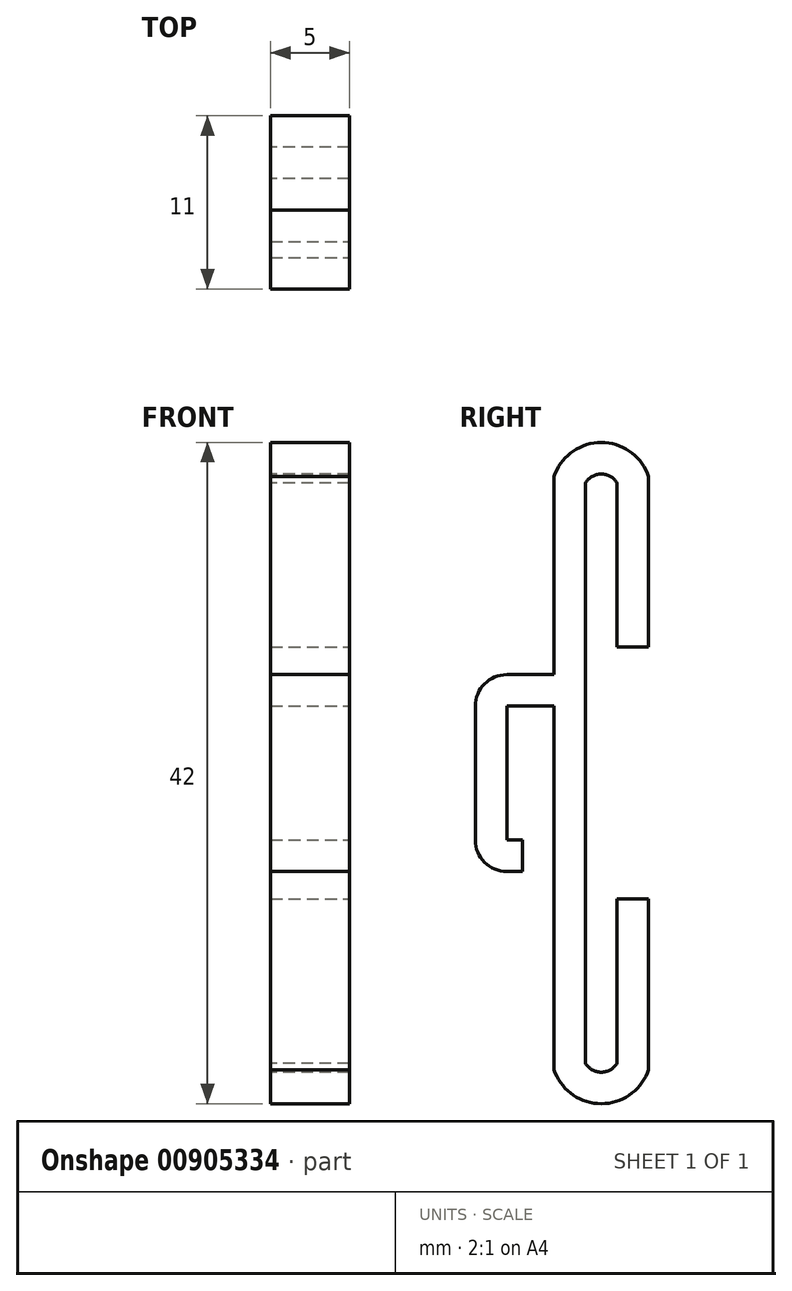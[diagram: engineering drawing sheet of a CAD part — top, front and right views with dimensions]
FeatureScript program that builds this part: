
annotation { "Feature Type Name" : "Feature", "Feature Type Description" : "" }
export const myFeature = defineFeature(function(context is Context, id is Id, definition is map)
    precondition{}
    {
        {
            assignVariable(context, id + "F0", {"name" : "thickness", "anyValue" : 2 * mm});
        }
        {
            var Q0;
            Q0=qCreatedBy(makeId("Right.planeOp"),FACE);
            var sketch = newSketch(context, id + "F1", { "sketchPlane" : qUnion([Q0])});
            skArc(sketch, "E0", {"start": v(4, 18.65) * mm, "mid": v(2, 20) * mm, "end": v(0, 18.65) * mm});
            skLineSegment(sketch, "E1", {"start": v(0, 18.65) * mm, "end": v(0, 0) * mm});
            skLineSegment(sketch, "E2", {"start": v(4, 18.65) * mm, "end": v(4, 8) * mm});
            skLineSegment(sketch, "E3", {"start": v(2, 20) * mm, "end": v(-23.66, 20) * mm, "construction": true});
            skLineSegment(sketch, "E4", {"start": v(2, 20) * mm, "end": v(20.62, 20) * mm, "construction": true});
            skLineSegment(sketch, "E5.MirrorCS", {"start": v(0, -18.65) * mm, "end": v(0, 0) * mm});
            skArc(sketch, "E6.MirrorCS", {"start": v(4, -18.65) * mm, "mid": v(2, -20) * mm, "end": v(0, -18.65) * mm});
            skLineSegment(sketch, "E7.MirrorCS", {"start": v(4, -18.65) * mm, "end": v(4, -8) * mm});
            skLineSegment(sketch, "E8", {"start": v(2, 20) * mm, "end": v(2, 17.84) * mm, "construction": true});
            skLineSegment(sketch, "E9", {"start": v(0, 18.65) * mm, "end": v(4, 18.65) * mm, "construction": true});
            skSolve(sketch);
        }
        {
            var Q0;
            Q0=qCreatedBy(makeId("Top.planeOp"),FACE);
            var sketch = newSketch(context, id + "F2", { "sketchPlane" : qUnion([Q0])});
            skLineSegment(sketch, "E10.bottom", {"start": v(-2.5, 1) * mm, "end": v(2.5, 1) * mm});
            skLineSegment(sketch, "E10.top", {"start": v(-2.5, -1) * mm, "end": v(2.5, -1) * mm});
            skLineSegment(sketch, "E10.left", {"start": v(-2.5, 1) * mm, "end": v(-2.5, -1) * mm});
            skLineSegment(sketch, "E10.right", {"start": v(2.5, 1) * mm, "end": v(2.5, -1) * mm});
            skLineSegment(sketch, "E11", {"start": v(2.5, 1) * mm, "end": v(-2.5, -1) * mm, "construction": true});
            skPoint(sketch, "E12", {"position": v(0, 0) * mm});
            skSolve(sketch);
        }
        {
            var Q0;
            Q0=makeQuery(id+"F2.imprint","IMPRINT",FACE,{"disambiguationData":[TD([[makeQuery(id+"F2.imprint","IMPRINT",EDGE,{"derivedFrom":sQuery(id+"F2.wireOp",EDGE,"E10.bottom")}),-1.0]])]});
            var Q1;
            Q1=sQuery(id+"F1.wireOp",EDGE,"E1");
            var Q2;
            Q2=sQuery(id+"F1.wireOp",EDGE,"E0");
            var Q3;
            Q3=sQuery(id+"F1.wireOp",EDGE,"E2");
            var Q4;
            Q4=sQuery(id+"F1.wireOp",EDGE,"E7.MirrorCS");
            var Q5;
            Q5=sQuery(id+"F1.wireOp",EDGE,"E6.MirrorCS");
            var Q6;
            Q6=sQuery(id+"F1.wireOp",EDGE,"E5.MirrorCS");
            sweep(context, id + "F3", {"profiles" : qUnion([Q0]), "path" : qUnion([Q1, Q2, Q3, Q4, Q5, Q6])});
        }
        {
            assignVariable(context, id + "F4", {"name" : "led_height", "anyValue" : 3 * mm});
        }
        {
            var Q0;
            Q0=makeQuery(id+"F3.opSweep","SWEPT_FACE",FACE,{"disambiguationData":[OSD([sQuery(id+"F1.wireOp",EDGE,"E1"),sQuery(id+"F2.wireOp",EDGE,"E10.top")])]});
            var sketch = newSketch(context, id + "F5", { "sketchPlane" : qUnion([Q0])});
            skLineSegment(sketch, "E13.bottom", {"start": v(-2.5, -6.25) * mm, "end": v(2.5, -6.25) * mm});
            skLineSegment(sketch, "E13.top", {"start": v(-2.5, 6.25) * mm, "end": v(2.5, 6.25) * mm});
            skLineSegment(sketch, "E13.left", {"start": v(-2.5, -6.25) * mm, "end": v(-2.5, 6.25) * mm});
            skLineSegment(sketch, "E13.right", {"start": v(2.5, -6.25) * mm, "end": v(2.5, 6.25) * mm});
            skLineSegment(sketch, "E14", {"start": v(-2.5, -6.25) * mm, "end": v(2.5, 6.25) * mm, "construction": true});
            skPoint(sketch, "E15", {"position": v(0, 0) * mm});
            skSolve(sketch);
        }
        {
            var Q0;
            Q0=makeQuery(id+"F5.imprint","IMPRINT",FACE,{"disambiguationData":[TD([[makeQuery(id+"F5.imprint","IMPRINT",EDGE,{"derivedFrom":sQuery(id+"F5.wireOp",EDGE,"E13.bottom")}),1.0]])]});
            extrude(context, id + "F6", {"entities" : qUnion([Q0]), "operationType" : NewBodyOperationType.ADD, "depth" : getVariable(context, 'led_height') + getVariable(context, 'thickness'), "offsetDistance" : 25 * mm});
        }
        {
            var Q0;
            Q0=makeQuery(id+"F6.boolean.opBoolean","MERGE",FACE,{"derivedFrom":[makeQuery(id+"F3.opSweep","SWEPT_FACE",FACE,{"disambiguationData":[OSD([sQuery(id+"F1.wireOp",EDGE,"E7.MirrorCS"),sQuery(id+"F2.wireOp",EDGE,"E10.right")])]}),makeQuery(id+"F6.opExtrude","SWEPT_FACE",FACE,{"disambiguationData":[OSD([sQuery(id+"F5.wireOp",EDGE,"E13.right")])]})]});
            var sketch = newSketch(context, id + "F7", { "sketchPlane" : qUnion([Q0])});
            skLineSegment(sketch, "E16.bottom", {"start": v(-4, -4.25) * mm, "end": v(-1, -4.25) * mm});
            skLineSegment(sketch, "E16.top", {"start": v(-4, 4.25) * mm, "end": v(-1, 4.25) * mm});
            skLineSegment(sketch, "E16.left", {"start": v(-4, -4.25) * mm, "end": v(-4, 4.25) * mm});
            skLineSegment(sketch, "E16.right", {"start": v(-1, -4.25) * mm, "end": v(-1, 4.25) * mm});
            skLineSegment(sketch, "E17", {"start": v(-4, -4.25) * mm, "end": v(-1, 4.25) * mm, "construction": true});
            skPoint(sketch, "E18", {"position": v(-2.5, 0) * mm});
            skSolve(sketch);
        }
        {
            var Q0;
            Q0=makeQuery(id+"F7.imprint","IMPRINT",FACE,{"disambiguationData":[TD([[makeQuery(id+"F7.imprint","IMPRINT",EDGE,{"derivedFrom":sQuery(id+"F7.wireOp",EDGE,"E16.bottom")}),1.0]])]});
            extrude(context, id + "F8", {"entities" : qUnion([Q0]), "operationType" : NewBodyOperationType.REMOVE, "endBound" : BoundingType.THROUGH_ALL, "oppositeDirection" : true, "depth" : 25 * mm, "offsetDistance" : 25 * mm});
        }
        {
            var Q0;
            Q0=makeQuery(id+"F6.opExtrude","SWEPT_FACE",FACE,{"disambiguationData":[OSD([sQuery(id+"F5.wireOp",EDGE,"E13.bottom")])]});
            var sketch = newSketch(context, id + "F9", { "sketchPlane" : qUnion([Q0])});
            skLineSegment(sketch, "E19.bottom", {"start": v(-2.5, 3) * mm, "end": v(2.5, 3) * mm});
            skLineSegment(sketch, "E19.top", {"start": v(-2.5, 1) * mm, "end": v(2.5, 1) * mm});
            skLineSegment(sketch, "E19.left", {"start": v(-2.5, 3) * mm, "end": v(-2.5, 1) * mm});
            skLineSegment(sketch, "E19.right", {"start": v(2.5, 3) * mm, "end": v(2.5, 1) * mm});
            skSolve(sketch);
        }
        {
            var Q0;
            Q0=makeQuery(id+"F9.imprint","IMPRINT",FACE,{"disambiguationData":[TD([[makeQuery(id+"F9.imprint","IMPRINT",EDGE,{"derivedFrom":sQuery(id+"F9.wireOp",EDGE,"E19.bottom")}),-1.0]])]});
            extrude(context, id + "F10", {"entities" : qUnion([Q0]), "operationType" : NewBodyOperationType.REMOVE, "endBound" : BoundingType.UP_TO_NEXT, "oppositeDirection" : true, "depth" : 25 * mm, "offsetDistance" : 25 * mm});
        }
        {
            var Q0;
            Q0=makeQuery(id+"F6.opExtrude","CAP_EDGE",EDGE,{"disambiguationData":[OSD([sQuery(id+"F5.wireOp",EDGE,"E13.top")])],"isStart":false});
            var Q1;
            Q1=makeQuery(id+"F6.opExtrude","CAP_EDGE",EDGE,{"disambiguationData":[OSD([sQuery(id+"F5.wireOp",EDGE,"E13.bottom")])],"isStart":false});
            fillet(context, id + "F11", {"entities" : qUnion([Q0, Q1]), "radius" : 2 * mm, "tangentPropagation" : true, "allowEdgeOverflow" : false});
        }
    });
